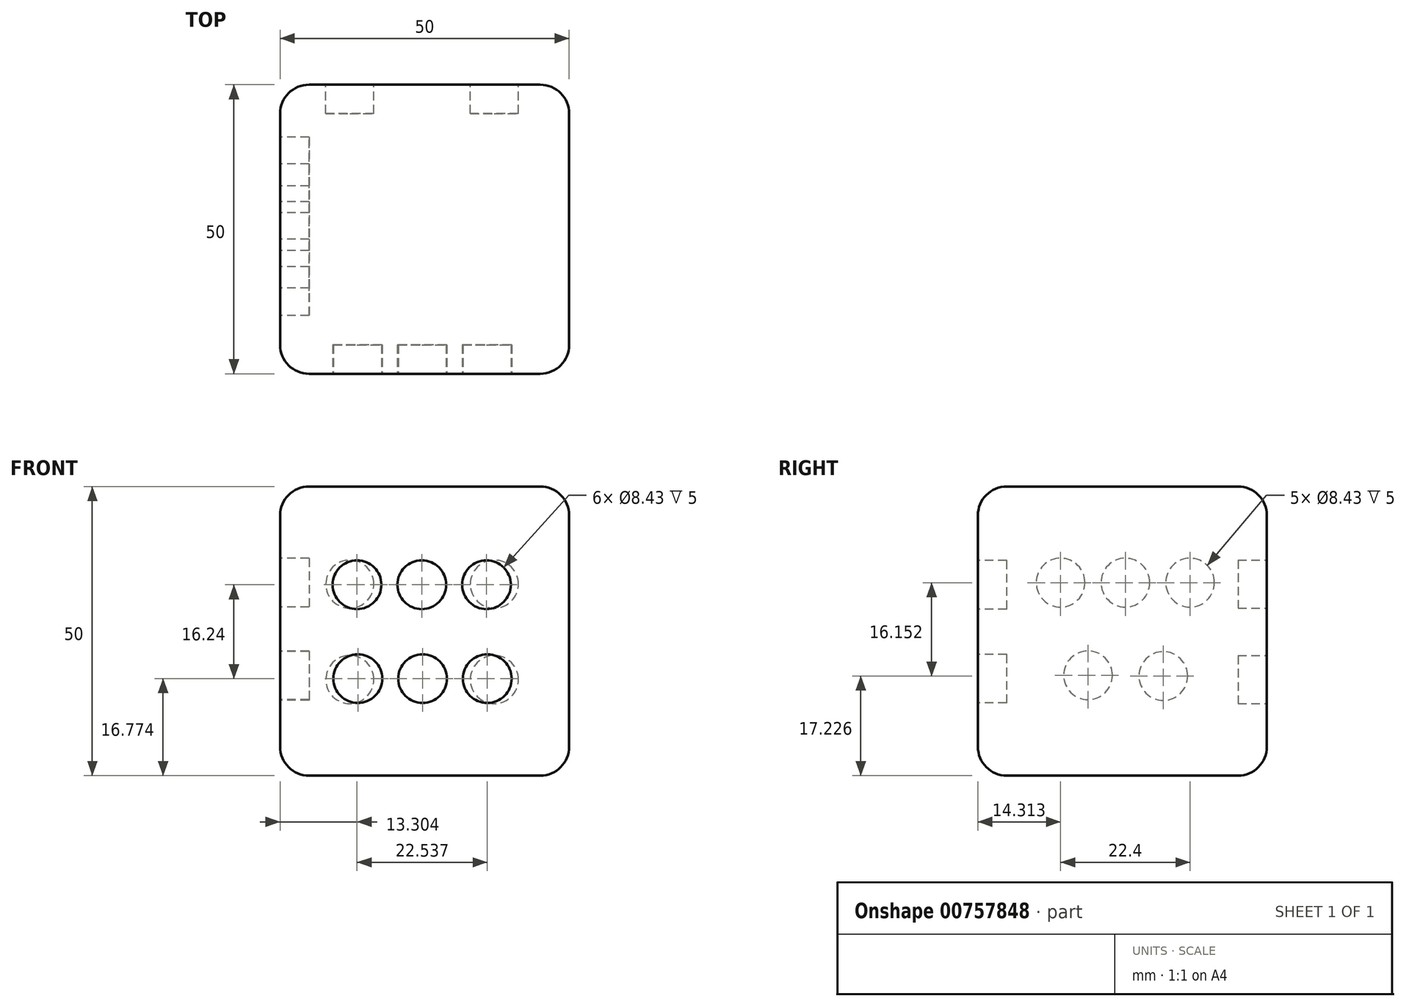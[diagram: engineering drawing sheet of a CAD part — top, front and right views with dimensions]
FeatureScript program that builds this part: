
annotation { "Feature Type Name" : "Feature", "Feature Type Description" : "" }
export const myFeature = defineFeature(function(context is Context, id is Id, definition is map)
    precondition{}
    {
        {
            var Q0;
            Q0=qCreatedBy(makeId("Top.planeOp"),FACE);
            var sketch = newSketch(context, id + "F0", { "sketchPlane" : qUnion([Q0])});
            skLineSegment(sketch, "E0.bottom", {"start": v(0, 0) * mm, "end": v(50, 0) * mm});
            skLineSegment(sketch, "E0.top", {"start": v(0, 50) * mm, "end": v(50, 50) * mm});
            skLineSegment(sketch, "E0.left", {"start": v(0, 0) * mm, "end": v(0, 50) * mm});
            skLineSegment(sketch, "E0.right", {"start": v(50, 0) * mm, "end": v(50, 50) * mm});
            skSolve(sketch);
        }
        {
            var Q0;
            Q0=makeQuery(id+"F0.imprint","IMPRINT",FACE,{"disambiguationData":[TD([[makeQuery(id+"F0.imprint","IMPRINT",EDGE,{"derivedFrom":sQuery(id+"F0.wireOp",EDGE,"E0.bottom")}),1.0]])]});
            extrude(context, id + "F1", {"entities" : qUnion([Q0]), "depth" : 50 * mm, "offsetDistance" : 25 * mm});
        }
        {
            var Q0;
            Q0=makeQuery(id+"F1.opExtrude","CAP_EDGE",EDGE,{"disambiguationData":[OSD([sQuery(id+"F0.wireOp",EDGE,"E0.bottom")])],"isStart":false});
            var Q1;
            Q1=makeQuery(id+"F1.opExtrude","SWEPT_EDGE",EDGE,{"disambiguationData":[OSD([sQuery(id+"F0.wireOp",EDGE,"E0.bottom"),sQuery(id+"F0.wireOp",EDGE,"E0.right")])]});
            var Q2;
            Q2=makeQuery(id+"F1.opExtrude","CAP_EDGE",EDGE,{"disambiguationData":[OSD([sQuery(id+"F0.wireOp",EDGE,"E0.bottom")])],"isStart":true});
            var Q3;
            Q3=makeQuery(id+"F1.opExtrude","SWEPT_EDGE",EDGE,{"disambiguationData":[OSD([sQuery(id+"F0.wireOp",EDGE,"E0.bottom"),sQuery(id+"F0.wireOp",EDGE,"E0.left")])]});
            var Q4;
            Q4=makeQuery(id+"F1.opExtrude","CAP_EDGE",EDGE,{"disambiguationData":[OSD([sQuery(id+"F0.wireOp",EDGE,"E0.left")])],"isStart":false});
            var Q5;
            Q5=makeQuery(id+"F1.opExtrude","SWEPT_EDGE",EDGE,{"disambiguationData":[OSD([sQuery(id+"F0.wireOp",EDGE,"E0.top"),sQuery(id+"F0.wireOp",EDGE,"E0.left")])]});
            var Q6;
            Q6=makeQuery(id+"F1.opExtrude","CAP_EDGE",EDGE,{"disambiguationData":[OSD([sQuery(id+"F0.wireOp",EDGE,"E0.left")])],"isStart":true});
            var Q7;
            Q7=makeQuery(id+"F1.opExtrude","CAP_EDGE",EDGE,{"disambiguationData":[OSD([sQuery(id+"F0.wireOp",EDGE,"E0.top")])],"isStart":false});
            var Q8;
            Q8=makeQuery(id+"F1.opExtrude","CAP_EDGE",EDGE,{"disambiguationData":[OSD([sQuery(id+"F0.wireOp",EDGE,"E0.right")])],"isStart":false});
            var Q9;
            Q9=makeQuery(id+"F1.opExtrude","SWEPT_EDGE",EDGE,{"disambiguationData":[OSD([sQuery(id+"F0.wireOp",EDGE,"E0.top"),sQuery(id+"F0.wireOp",EDGE,"E0.right")])]});
            var Q10;
            Q10=makeQuery(id+"F1.opExtrude","CAP_EDGE",EDGE,{"disambiguationData":[OSD([sQuery(id+"F0.wireOp",EDGE,"E0.top")])],"isStart":true});
            var Q11;
            Q11=makeQuery(id+"F1.opExtrude","CAP_EDGE",EDGE,{"disambiguationData":[OSD([sQuery(id+"F0.wireOp",EDGE,"E0.right")])],"isStart":true});
            fillet(context, id + "F2", {"entities" : qUnion([Q0, Q1, Q2, Q3, Q4, Q5, Q6, Q7, Q8, Q9, Q10, Q11]), "radius" : 5 * mm, "tangentPropagation" : true, "allowEdgeOverflow" : false});
        }
        {
            var Q0;
            Q0=makeQuery(id+"F1.opExtrude","SWEPT_FACE",FACE,{"disambiguationData":[OSD([sQuery(id+"F0.wireOp",EDGE,"E0.bottom")])]});
            var sketch = newSketch(context, id + "F3", { "sketchPlane" : qUnion([Q0])});
            skCircle(sketch, "E1", {"center": v(13.3, 33.01) * mm, "radius": 4.22 * mm});
            skCircle(sketch, "E2.1.0.0", {"center": v(24.5, 33.01) * mm, "radius": 4.22 * mm});
            skCircle(sketch, "E2.2.0.0", {"center": v(35.7, 33.01) * mm, "radius": 4.22 * mm});
            skLineSegment(sketch, "E2.direction1", {"start": v(13.3, 33.01) * mm, "end": v(24.5, 33.01) * mm, "construction": true});
            skCircle(sketch, "E3", {"center": v(13.44, 16.77) * mm, "radius": 4.22 * mm});
            skCircle(sketch, "E4.1.0.0", {"center": v(24.64, 16.77) * mm, "radius": 4.22 * mm});
            skCircle(sketch, "E4.2.0.0", {"center": v(35.84, 16.77) * mm, "radius": 4.22 * mm});
            skSolve(sketch);
        }
        {
            var Q0;
            Q0=makeQuery(id+"F3.imprint","IMPRINT",FACE,{"disambiguationData":[TD([[makeQuery(id+"F3.imprint","IMPRINT",EDGE,{"derivedFrom":sQuery(id+"F3.wireOp",EDGE,"E1")}),1.0]])]});
            var Q1;
            Q1=makeQuery(id+"F3.imprint","IMPRINT",FACE,{"disambiguationData":[TD([[makeQuery(id+"F3.imprint","IMPRINT",EDGE,{"derivedFrom":sQuery(id+"F3.wireOp",EDGE,"E2.1.0.0")}),1.0]])]});
            var Q2;
            Q2=makeQuery(id+"F3.imprint","IMPRINT",FACE,{"disambiguationData":[TD([[makeQuery(id+"F3.imprint","IMPRINT",EDGE,{"derivedFrom":sQuery(id+"F3.wireOp",EDGE,"E2.2.0.0")}),1.0]])]});
            var Q3;
            Q3=makeQuery(id+"F3.imprint","IMPRINT",FACE,{"disambiguationData":[TD([[makeQuery(id+"F3.imprint","IMPRINT",EDGE,{"derivedFrom":sQuery(id+"F3.wireOp",EDGE,"E3")}),1.0]])]});
            var Q4;
            Q4=makeQuery(id+"F3.imprint","IMPRINT",FACE,{"disambiguationData":[TD([[makeQuery(id+"F3.imprint","IMPRINT",EDGE,{"derivedFrom":sQuery(id+"F3.wireOp",EDGE,"E4.1.0.0")}),1.0]])]});
            var Q5;
            Q5=makeQuery(id+"F3.imprint","IMPRINT",FACE,{"disambiguationData":[TD([[makeQuery(id+"F3.imprint","IMPRINT",EDGE,{"derivedFrom":sQuery(id+"F3.wireOp",EDGE,"E4.2.0.0")}),1.0]])]});
            extrude(context, id + "F4", {"entities" : qUnion([Q0, Q1, Q2, Q3, Q4, Q5]), "operationType" : NewBodyOperationType.REMOVE, "oppositeDirection" : true, "depth" : 5 * mm, "offsetDistance" : 25 * mm});
        }
        {
            var Q0;
            Q0=makeQuery(id+"F1.opExtrude","SWEPT_FACE",FACE,{"disambiguationData":[OSD([sQuery(id+"F0.wireOp",EDGE,"E0.left")])]});
            var sketch = newSketch(context, id + "F5", { "sketchPlane" : qUnion([Q0])});
            skCircle(sketch, "E5", {"center": v(-36.71, 33.38) * mm, "radius": 4.22 * mm});
            skCircle(sketch, "E6.1.0.0", {"center": v(-25.51, 33.38) * mm, "radius": 4.22 * mm});
            skCircle(sketch, "E6.2.0.0", {"center": v(-14.31, 33.38) * mm, "radius": 4.22 * mm});
            skCircle(sketch, "E7", {"center": v(-32.08, 17.23) * mm, "radius": 4.22 * mm});
            skCircle(sketch, "E8.2.0.0", {"center": v(-19.06, 17.34) * mm, "radius": 4.22 * mm});
            skSolve(sketch);
        }
        {
            var Q0;
            Q0=makeQuery(id+"F5.imprint","IMPRINT",FACE,{"disambiguationData":[TD([[makeQuery(id+"F5.imprint","IMPRINT",EDGE,{"derivedFrom":sQuery(id+"F5.wireOp",EDGE,"E5")}),1.0]])]});
            var Q1;
            Q1=makeQuery(id+"F5.imprint","IMPRINT",FACE,{"disambiguationData":[TD([[makeQuery(id+"F5.imprint","IMPRINT",EDGE,{"derivedFrom":sQuery(id+"F5.wireOp",EDGE,"E6.1.0.0")}),1.0]])]});
            var Q2;
            Q2=makeQuery(id+"F5.imprint","IMPRINT",FACE,{"disambiguationData":[TD([[makeQuery(id+"F5.imprint","IMPRINT",EDGE,{"derivedFrom":sQuery(id+"F5.wireOp",EDGE,"E6.2.0.0")}),1.0]])]});
            var Q3;
            Q3=makeQuery(id+"F5.imprint","IMPRINT",FACE,{"disambiguationData":[TD([[makeQuery(id+"F5.imprint","IMPRINT",EDGE,{"derivedFrom":sQuery(id+"F5.wireOp",EDGE,"E7")}),1.0]])]});
            var Q4;
            Q4=makeQuery(id+"F5.imprint","IMPRINT",FACE,{"disambiguationData":[TD([[makeQuery(id+"F5.imprint","IMPRINT",EDGE,{"derivedFrom":sQuery(id+"F5.wireOp",EDGE,"E8.2.0.0")}),1.0]])]});
            extrude(context, id + "F6", {"entities" : qUnion([Q0, Q1, Q2, Q3, Q4]), "operationType" : NewBodyOperationType.REMOVE, "oppositeDirection" : true, "depth" : 5 * mm, "offsetDistance" : 25 * mm});
        }
        {
            var Q0;
            Q0=makeQuery(id+"F1.opExtrude","SWEPT_FACE",FACE,{"disambiguationData":[OSD([sQuery(id+"F0.wireOp",EDGE,"E0.top")])]});
            var sketch = newSketch(context, id + "F7", { "sketchPlane" : qUnion([Q0])});
            skCircle(sketch, "E9", {"center": v(-37.06, 33.11) * mm, "radius": 4.16 * mm});
            skCircle(sketch, "E10.0.1.0", {"center": v(-37.06, 16.61) * mm, "radius": 4.16 * mm});
            skCircle(sketch, "E10.1.0.0", {"center": v(-12.06, 33.11) * mm, "radius": 4.16 * mm});
            skCircle(sketch, "E10.1.1.0", {"center": v(-12.06, 16.61) * mm, "radius": 4.16 * mm});
            skLineSegment(sketch, "E10.direction1", {"start": v(-37.06, 33.11) * mm, "end": v(-12.06, 33.11) * mm, "construction": true});
            skLineSegment(sketch, "E10.direction2", {"start": v(-37.06, 33.11) * mm, "end": v(-37.06, 16.61) * mm, "construction": true});
            skSolve(sketch);
        }
        {
            var Q0;
            Q0=makeQuery(id+"F7.imprint","IMPRINT",FACE,{"disambiguationData":[TD([[makeQuery(id+"F7.imprint","IMPRINT",EDGE,{"derivedFrom":sQuery(id+"F7.wireOp",EDGE,"E10.1.1.0")}),1.0]])]});
            var Q1;
            Q1=makeQuery(id+"F7.imprint","IMPRINT",FACE,{"disambiguationData":[TD([[makeQuery(id+"F7.imprint","IMPRINT",EDGE,{"derivedFrom":sQuery(id+"F7.wireOp",EDGE,"E10.0.1.0")}),1.0]])]});
            var Q2;
            Q2=makeQuery(id+"F7.imprint","IMPRINT",FACE,{"disambiguationData":[TD([[makeQuery(id+"F7.imprint","IMPRINT",EDGE,{"derivedFrom":sQuery(id+"F7.wireOp",EDGE,"E10.1.0.0")}),1.0]])]});
            var Q3;
            Q3=makeQuery(id+"F7.imprint","IMPRINT",FACE,{"disambiguationData":[TD([[makeQuery(id+"F7.imprint","IMPRINT",EDGE,{"derivedFrom":sQuery(id+"F7.wireOp",EDGE,"E9")}),1.0]])]});
            extrude(context, id + "F8", {"entities" : qUnion([Q0, Q1, Q2, Q3]), "operationType" : NewBodyOperationType.REMOVE, "oppositeDirection" : true, "depth" : 5 * mm, "offsetDistance" : 25 * mm});
        }
    });
